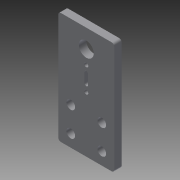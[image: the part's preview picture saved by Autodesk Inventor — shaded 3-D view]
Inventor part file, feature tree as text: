
AUTODESK INVENTOR PART (.ipt)
format: ipt  version: 2015 SP1 (Build 190203100, 203)  size: 124,416 bytes
history: native  units: in
note: dims shown in document units (in); Inventor stores cm internally (conversion verified against a paired STEP export)
features: extrude x1, fillet x1, sketch x1
ambient origin geometry x8: Origin, YZ Plane, XZ Plane, XY Plane, X Axis, Y Axis, Z Axis, Center Point
bodies: Body1 (feature_tree)
feature tree (3):
  extrude  "Extrusion3"  Depth=1.7717in
  fillet  "Fillet2"  Radius=0.2756in
  sketch  "Sketch1"  dims[d2=3.5433in d3=1.7717in d4=0.2756in d5=0.2756in d6=0.2756in d7=0.2756in d9=0.3937in d10=0.9843in d11=0.7874in d12=0.4724in d13=0.5906in d17=0.1299in d18=0.1299in d19=0.748in d20=0.2992in d21=0.1181in d22=0.2362in d23=0.0in d24=0.0787in]
